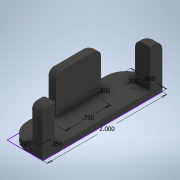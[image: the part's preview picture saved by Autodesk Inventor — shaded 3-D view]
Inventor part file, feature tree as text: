
AUTODESK INVENTOR PART (.ipt)
format: ipt  version: 2020 (Build 240168000, 168)  size: 169,984 bytes
history: native  units: in
note: dims shown in document units (in); Inventor stores cm internally (conversion verified against a paired STEP export)
features: extrude x2, fillet x2, sketch x1
ambient origin geometry x8: Origin, YZ Plane, XZ Plane, XY Plane, X Axis, Y Axis, Z Axis, Center Point
bodies: Solid1 (feature_tree)
feature tree (5):
  sketch  "Sketch1"  dims[d0=0.6in d1=2.0in d2=0.25in d3=0.2in d4=0.2in d8=0.2in d9=0.75in d10=0.75in d11=0.0in d12=0.1in d13=0.0in d14=0.35in d15=0.125in]
  extrude  "Extrusion1"  Depth=2.0in
  extrude  "Extrusion2"  Depth=0.25in
  fillet  "Fillet1"  Radius=0.2in
  fillet  "Fillet2"  Radius=0.2in
